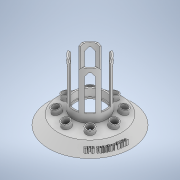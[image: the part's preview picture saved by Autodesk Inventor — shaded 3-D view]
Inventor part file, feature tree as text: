
AUTODESK INVENTOR PART (.ipt)
format: ipt  version: 2022 (Build 260153000, 153)  size: 1,102,848 bytes
history: native  units: in
note: dims shown in document units (in); Inventor stores cm internally (conversion verified against a paired STEP export)
features: sketch x11, extrude x7, revolve x4, pattern_circular x4, plane x1, emboss x1, projected_geometry x1
ambient origin geometry x8: Origin, YZ Plane, XZ Plane, XY Plane, X Axis, Y Axis, Z Axis, Center Point
bodies: Solid1 (feature_tree)
feature tree (29):
  extrude  "Extrusion1"  Depth=0.0964in
  revolve  "Revolution1"  [1 undecoded]
  plane  "Work Plane1"
  extrude  "Extrusion3"  Depth=2.3622in
  extrude  "Extrusion4"  TaperAngle=0.0deg  [1 undecoded]
  extrude  "Extrusion5"  Depth=2.3622in
  revolve  "Revolution2"  [1 undecoded]
  pattern_circular  "Circular Pattern1"  Count=10  [1 undecoded]
  extrude  "Extrusion6"  Depth=0.315in
  pattern_circular  "Circular Pattern2"  Count=8 Angle=360.0deg
  extrude  "Extrusion7"  Depth=0.3937in
  revolve  "Revolution3"  [1 undecoded]
  revolve  "Revolution4"  [1 undecoded]
  pattern_circular  "Circular Pattern3"  [2 undecoded]
  extrude  "Extrusion8"  Depth=0.6299in
  pattern_circular  "Circular Pattern4"  [2 undecoded]
  emboss  "Emboss4"
  sketch  "Sketch1"  dims[d2=0.1969in d3=0.0in d8=0.0964in]
  sketch  "Sketch4"  dims[d9=90.0deg d10=0.5315in]
  sketch  "Sketch5"  dims[d11=2.5984in d12=2.3622in]
  sketch  "Sketch6"  dims[d13=0.1969in d14=0.0in d15=0.0in]
  sketch  "Sketch7"  dims[d16=2.5197in d17=2.3622in]
  sketch  "Sketch9"  dims[d18=0.0787in d19=0.0in d22=0.1181in d23=3.937in d24=0.0in]
  sketch  "Sketch13"  dims[d25=0.0591in d26=0.0in d35=0.315in]
  sketch  "Sketch14"  dims[d36=90.0deg d37=3.1496in d38=360.0deg]
  sketch  "Sketch16"  dims[d40=5.2756in d41=0.3937in]
  sketch  "Sketch17"  dims[d42=0.0825in d43=0.0in d44=0.0in]
  sketch  "Sketch20"  dims[d45=3.1496in d46=360.0deg d49=0.5906in d50=0.0in d51=0.6299in d52=4.5669in d53=5.0591in d54=4.626in d55=0.1575in d56=0.0in d57=0.0in d60=0.1969in d61=0.1969in d62=0.1969in d63=90.0deg d69=0.3937in d70=0.0825in d71=0.0in d72=90.0deg d73=0.0787in d74=0.2797in d75=0.0in d76=0.378in d77=3.1496in d78=360.0deg d81=0.5906in d82=0.0in d83=0.7874in d85=0.0in d86=0.0in d87=1.5748in d88=360.0deg d98=0.0787in d102=0.315in d103=0.1969in d104=0.1969in d106=0.1969in d107=0.1969in d108=0.0787in d109=0.0in d110=0.315in d111=2.6772in d112=2.6772in d113=0.0787in d68=0.0344in]
  projected_geometry  "Project Cut Edges1"
note: 10 required parameter values undecoded (feature->parameter linkage not recoverable at this tier; creation-order binding heuristic only, values carry confidence <= 0.55)